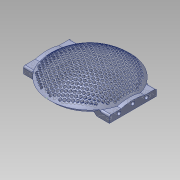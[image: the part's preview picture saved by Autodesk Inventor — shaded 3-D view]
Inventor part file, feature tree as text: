
AUTODESK INVENTOR PART (.ipt)
format: ipt  version: 2015 (Build 190159000, 159)  size: 3,254,272 bytes
history: native  units: in
note: dims shown in document units (in); Inventor stores cm internally (conversion verified against a paired STEP export)
features: sketch x7, extrude x4, plane x3, mirror x3, other x2, revolve x2, fillet x1, imported_body x1
ambient origin geometry x8: Origin, YZ Plane, XZ Plane, XY Plane, X Axis, Y Axis, Z Axis, Center Point
bodies: Body1 (feature_tree)
feature tree (23):
  other  "Boss-Extrude1"
  other  "102_CellScopeDomeTop_80deg_v0.ipt1"
  plane  "Work Plane1"
  plane  "Work Plane4"
  revolve  "Revolution1"  [1 undecoded]
  extrude  "Extrusion8"  Depth=1.8898in
  extrude  "Extrusion9"  Depth=0.3937in TaperAngle=0.0deg
  mirror  "Mirror4"
  extrude  "Extrusion10"  Depth=0.3937in
  fillet  "Fillet8"  Radius=0.1562in
  sketch  "Sketch16"  dims[d67=0.315in d69=0.3937in d70=0.0in]
  mirror  "Mirror5"
  extrude  "Extrusion11"  Depth=0.3543in
  revolve  "Revolution2"  [1 undecoded]
  mirror  "Mirror6"
  imported_body  "Base1"
  sketch  "Sketch13"  dims[d6=1.4961in d63=1.9685in d64=1.4961in]
  sketch  "Sketch14"  dims[d65=2.1654in d66=1.8898in]
  plane  "Work Plane5"
  sketch  "Sketch17"  dims[d71=0.3937in d72=0.0in d73=0.0787in d74=0.1562in]
  sketch  "Sketch19"  dims[d75=1.2598in d76=0.3543in]
  sketch  "Sketch22"  dims[d77=0.1875in d78=0.0in d79=0.1562in]
  sketch  "Sketch23"  dims[d80=1.7717in d81=3.5433in d82=0.1875in d83=0.0in d84=0.5118in d85=2.5984in d86=0.3436in d87=90.0deg d88=90.0deg]
note: 2 required parameter values undecoded (feature->parameter linkage not recoverable at this tier; creation-order binding heuristic only, values carry confidence <= 0.55)
